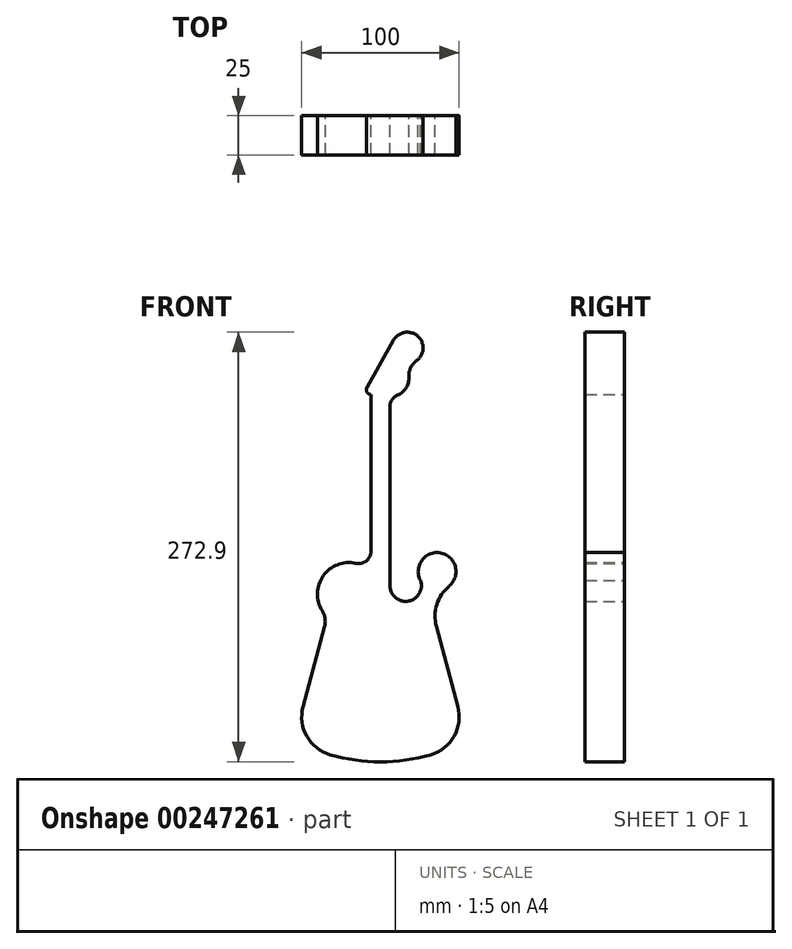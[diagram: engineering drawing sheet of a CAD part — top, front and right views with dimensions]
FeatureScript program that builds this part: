
annotation { "Feature Type Name" : "Feature", "Feature Type Description" : "" }
export const myFeature = defineFeature(function(context is Context, id is Id, definition is map)
    precondition{}
    {
        {
            var Q0;
            Q0=qCreatedBy(makeId("Front.planeOp"),FACE);
            var sketch = newSketch(context, id + "F0", { "sketchPlane" : qUnion([Q0])});
            skLineSegment(sketch, "E0", {"start": v(0, 181.97) * mm, "end": v(0, -63.57) * mm, "construction": true});
            skLineSegment(sketch, "E1", {"start": v(-72.28, -53.82) * mm, "end": v(62.27, -53.82) * mm, "construction": true});
            skArc(sketch, "E2", {"start": v(-49.15, -47.35) * mm, "mid": v(-46.77, -66.1) * mm, "end": v(-31.94, -77.83) * mm});
            skArc(sketch, "E3", {"start": v(31.94, -77.83) * mm, "mid": v(46.77, -66.1) * mm, "end": v(49.15, -47.35) * mm});
            skLineSegment(sketch, "E4", {"start": v(-49.15, -47.35) * mm, "end": v(-35.47, 3.7) * mm});
            skArc(sketch, "E5", {"start": v(-15.71, 43.72) * mm, "mid": v(-36.35, 35.7) * mm, "end": v(-36.95, 13.57) * mm});
            skLineSegment(sketch, "E6", {"start": v(-6, 51.53) * mm, "end": v(-6, 150.98) * mm});
            skArc(sketch, "E7", {"start": v(-35.47, 3.7) * mm, "mid": v(-35.18, 8.79) * mm, "end": v(-36.95, 13.57) * mm});
            skArc(sketch, "E8", {"start": v(-31.94, -77.83) * mm, "mid": v(0, -82.36) * mm, "end": v(31.94, -77.83) * mm});
            skArc(sketch, "E9", {"start": v(-15.71, 43.72) * mm, "mid": v(-8.99, 45.3) * mm, "end": v(-6, 51.53) * mm});
            skLineSegment(sketch, "E10", {"start": v(6, 143.13) * mm, "end": v(6, 29.54) * mm});
            skLineSegment(sketch, "E11", {"start": v(16, 19.54) * mm, "end": v(48.56, 19.54) * mm, "construction": true});
            skArc(sketch, "E12", {"start": v(43.95, 29.55) * mm, "mid": v(38.1, 50.36) * mm, "end": v(25.44, 32.84) * mm});
            skArc(sketch, "E13", {"start": v(6, 29.54) * mm, "mid": v(18.52, 19.86) * mm, "end": v(24.73, 34.42) * mm});
            skLineSegment(sketch, "E14.MirrorCS", {"start": v(49.15, -47.35) * mm, "end": v(35.47, 3.7) * mm});
            skArc(sketch, "E15", {"start": v(43.43, 29.1) * mm, "mid": v(35.76, 17.45) * mm, "end": v(35.52, 3.5) * mm});
            skLineSegment(sketch, "E16", {"start": v(-17.07, 150.98) * mm, "end": v(41.14, 150.98) * mm, "construction": true});
            skLineSegment(sketch, "E17", {"start": v(0, 150.98) * mm, "end": v(22.14, 189.33) * mm, "construction": true});
            skArc(sketch, "E18", {"start": v(0, 151.14) * mm, "mid": v(0.13, 151.06) * mm, "end": v(0.27, 150.98) * mm});
            skArc(sketch, "E19", {"start": v(22.96, 172.46) * mm, "mid": v(23.72, 188.01) * mm, "end": v(8.36, 185.47) * mm});
            skArc(sketch, "E20", {"start": v(-8.61, 155.46) * mm, "mid": v(-8.6, 152.47) * mm, "end": v(-6, 150.98) * mm});
            skLineSegment(sketch, "E21", {"start": v(-8.61, 155.46) * mm, "end": v(8.36, 185.47) * mm});
            skArc(sketch, "E22", {"start": v(22.96, 172.46) * mm, "mid": v(19.2, 167.92) * mm, "end": v(18.05, 162.13) * mm});
            skArc(sketch, "E23.trimOffspring", {"start": v(27.78, 150.98) * mm, "mid": v(30.03, 150.77) * mm, "end": v(32.29, 150.98) * mm});
            skArc(sketch, "E24.trimOffspring", {"start": v(43.43, 29.1) * mm, "mid": v(43.69, 29.32) * mm, "end": v(43.95, 29.55) * mm});
            skArc(sketch, "E25", {"start": v(15.53, 150.98) * mm, "mid": v(8.91, 149.3) * mm, "end": v(6, 143.13) * mm});
            skArc(sketch, "E26.trimOffspring", {"start": v(10.83, 150.47) * mm, "mid": v(16.27, 155.17) * mm, "end": v(18.05, 162.13) * mm});
            skSolve(sketch);
        }
        {
            var Q0;
            Q0 = qSketchRegion(id + "F0", true);
            extrude(context, id + "F1", {"entities" : qUnion([Q0]), "depth" : 25 * mm});
        }
    });
